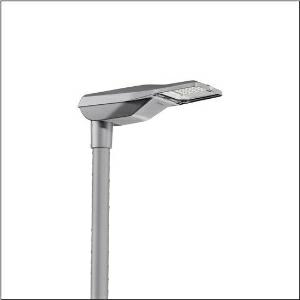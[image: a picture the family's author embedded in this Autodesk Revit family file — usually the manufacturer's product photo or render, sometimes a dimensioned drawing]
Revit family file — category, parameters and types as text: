
# Revit family: streetlight_sl_21_iq_micro___st1_5a_5xe1p31g08cb_4914
name_source: partatom
category: Lighting Fixtures
units: mm (PartAtom-declared; Revit-internal decimal feet)

## family parameters
Cut with Voids When Loaded = No
Host = Face
Light Source = No
Part Type = Normal
Room Calculation Point = No
Round Connector Dimension = Use Diameter
Shared = No

## types (1)
- --- (1 x LED, 2820 lm, 19.4 W, 3000K)
    Apparent Load = 19 VA
    CIE Flux Codes = 22 53 95 100 100
    Color Rendering = 70
    Color Temperature = 3000K
    Default Elevation = 1800 mm
    Description = Streetlight SL 21 iQ micro, mast luminaire, primary light control with lens, of PMMA, primary optical cover: cover, of toughened safety glass, transparent, light distribution: ST1.5a, light emission: direct distribution, primary light characteristic: asymmetric, installation type: post-top, side-entry, LED, High Power LED, rated luminous flux: 2.820lm, luminous efficacy: 145lm/W, light colour: 730, colour temperature: 3000K, control gear: iQ Street-Remote, control: Street-Remote, Auto-Match, Temp-Guard, Lumen-Switch, Night-Set, Smart-Wire, Light-Fading, Desk-Remote (wireless, voltage-free reading and setting of iQ features in the workshop via application-optimized NFC function/RFID function), optimised constant luminous flux control (CLO 2.0), pre-setting: linear dimming characteristic, mains connection: 220..240V, AC, 50/60Hz, start of lifetime: 19W, end of service life: 20W, reduction: 10W, luminaire housing, of diecast aluminium, powder-coated, Siteco® metallic grey (DB 702S), corrosivity category C5 mid according to DIN EN ISO 12944, please order mast flange separately, inclination adjustable: 0°, 5°, 10°, 15°, sealing non-destructively replaceable, multi-level sealing system, length: 528mm, width: 235mm, height: 110mm, mast flange for spigot size: 42mm (side-entry): 5XC10008XM4, 60/48mm (side-entry/post-top): 5XC10108XM2, 76/60mm (side-entry/post-top): 5XC10108XM1, protection rating (complete): IP66, insulation class (complete): insulation class II (safety insulation), certification: CE, ENEC, ENEC+, VDE, impact resistance: IK10, permissible operating ambient temperature for outdoor applications: -40..+50°C, standard-compliant lighting for roads and squares, packaging unit: 1 piece

Light Distribution: ST1.5a
    Height = 110 mm
    Lamp = 1 x LED
    Lamp Light Flux = 2820 lm
    Lamp Power = 19.4 W
    Lamp count = 1
    Length = 528 mm
    Luminous efficacy = 145 lm/W
    Manufacturer = Siteco
    ModVariant = No
    Model = 5XE1P31G08CB
    Number of Poles = 1
    OnlyDefault = Yes
    Power Factor = 1
    Product Name = Streetlight SL 21 iQ micro | ST1.5a
    Product group = mast luminaire | pylon top
    ProductGroupID = 6100
    Protection Class = Protection class II
    Protection Degree = IP 66
    RLX_Detail_Level = 1
    RLX_Emergency_Light_Flux = 0 lm
    RLX_Emergency_Type = 0
    RLX_Emergency_Type_DB = No
    RlxData = <blob elided: 102929 chars, md5=752dcfa8>
    Socket = socket
    Standby Power = 0 W
    System Light Flux = 2820 lm
    System Power = 19 W
    Type Comments = factory setting: luminous flux: 100 % | dim-lin: 254 | 387 mA
    Type Image = l_1006881.jpg
    URL = http://relux.com
    VarID = @adj_159551
    Voltage = 0 V
    Weight = 0.00 kg
    Width = 235 mm

## geometry (parser evidence)
native form markers: Blend x4, Sweep x11
no freeform markers — native parametric forms only
